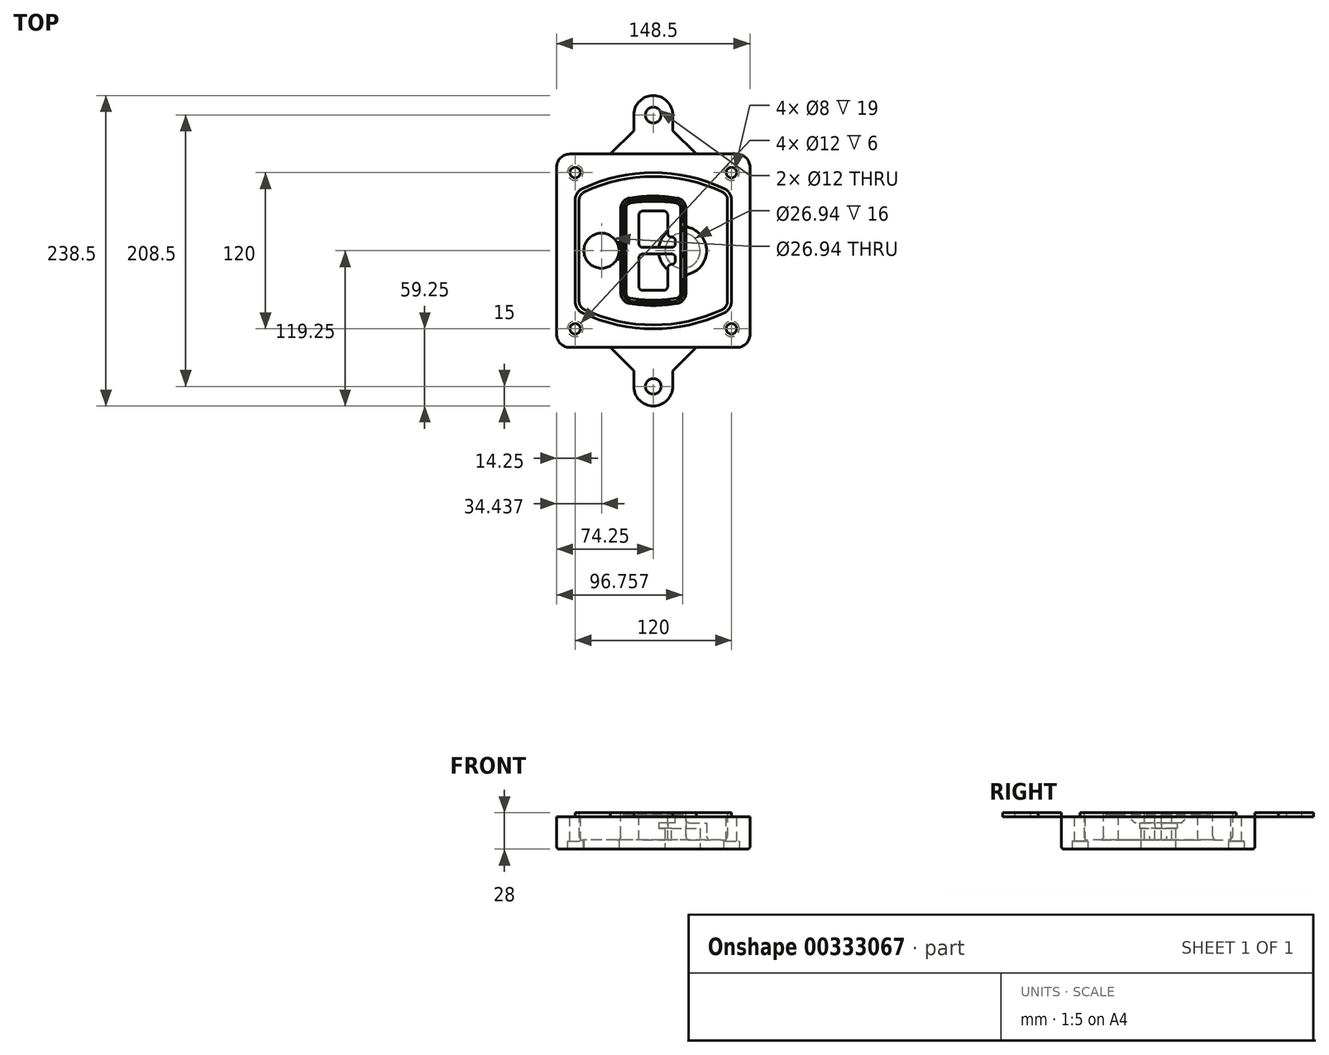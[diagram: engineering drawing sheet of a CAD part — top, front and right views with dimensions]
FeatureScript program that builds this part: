
annotation { "Feature Type Name" : "Feature", "Feature Type Description" : "" }
export const myFeature = defineFeature(function(context is Context, id is Id, definition is map)
    precondition{}
    {
        {
            var Q0;
            Q0=qCreatedBy(makeId("Top.planeOp"),FACE);
            var sketch = newSketch(context, id + "F0", { "sketchPlane" : qUnion([Q0])});
            skPoint(sketch, "E0.rect.middle", {"position": v(0, 0) * mm});
            skLineSegment(sketch, "E1.bottom", {"start": v(-64.25, -74.25) * mm, "end": v(64.25, -74.25) * mm});
            skLineSegment(sketch, "E1.top", {"start": v(-64.25, 74.25) * mm, "end": v(64.25, 74.25) * mm});
            skLineSegment(sketch, "E1.left", {"start": v(-74.25, -64.25) * mm, "end": v(-74.25, 64.25) * mm});
            skLineSegment(sketch, "E1.right", {"start": v(74.25, -64.25) * mm, "end": v(74.25, 64.25) * mm});
            skLineSegment(sketch, "E2", {"start": v(-74.25, 74.25) * mm, "end": v(74.25, -74.25) * mm, "construction": true});
            skLineSegment(sketch, "E3", {"start": v(74.25, 74.25) * mm, "end": v(-74.25, -74.25) * mm, "construction": true});
            skCircle(sketch, "E4", {"center": v(-60, 60) * mm, "radius": 4 * mm});
            skCircle(sketch, "E5", {"center": v(60, 60) * mm, "radius": 4 * mm});
            skCircle(sketch, "E6", {"center": v(60, -60) * mm, "radius": 4 * mm});
            skCircle(sketch, "E7", {"center": v(-60, -60) * mm, "radius": 4 * mm});
            skLineSegment(sketch, "E8", {"start": v(-60, 60) * mm, "end": v(60, 60) * mm, "construction": true});
            skLineSegment(sketch, "E9", {"start": v(60, 60) * mm, "end": v(60, -60) * mm, "construction": true});
            skLineSegment(sketch, "E10", {"start": v(60, -60) * mm, "end": v(-60, -60) * mm, "construction": true});
            skLineSegment(sketch, "E11", {"start": v(-60, -60) * mm, "end": v(-60, 60) * mm, "construction": true});
            skLineSegment(sketch, "E12", {"start": v(-60, 38.83) * mm, "end": v(-60, -38.83) * mm});
            skLineSegment(sketch, "E13", {"start": v(60, 38.83) * mm, "end": v(60, -38.83) * mm});
            skArc(sketch, "E14", {"start": v(54.26, 47.88) * mm, "mid": v(0, 60) * mm, "end": v(-54.26, 47.88) * mm});
            skArc(sketch, "E15", {"start": v(-54.26, -47.88) * mm, "mid": v(0, -60) * mm, "end": v(54.26, -47.88) * mm});
            skLineSegment(sketch, "E16", {"start": v(-60, 0) * mm, "end": v(60, 0) * mm, "construction": true});
            skPoint(sketch, "E17.visualSharp", {"position": v(-60, -45) * mm});
            skArc(sketch, "E17.filletArc", {"start": v(-60, -38.83) * mm, "mid": v(-58.44, -44.2) * mm, "end": v(-54.26, -47.88) * mm});
            skPoint(sketch, "E18.visualSharp", {"position": v(-60, 45) * mm});
            skArc(sketch, "E18.filletArc", {"start": v(-54.26, 47.88) * mm, "mid": v(-58.44, 44.2) * mm, "end": v(-60, 38.83) * mm});
            skPoint(sketch, "E19.visualSharp", {"position": v(60, 45) * mm});
            skArc(sketch, "E19.filletArc", {"start": v(60, 38.83) * mm, "mid": v(58.44, 44.2) * mm, "end": v(54.26, 47.88) * mm});
            skPoint(sketch, "E20.visualSharp", {"position": v(60, -45) * mm});
            skArc(sketch, "E20.filletArc", {"start": v(54.26, -47.88) * mm, "mid": v(58.44, -44.2) * mm, "end": v(60, -38.83) * mm});
            skPoint(sketch, "E21.visualSharp", {"position": v(-74.25, 74.25) * mm});
            skArc(sketch, "E21.filletArc", {"start": v(-64.25, 74.25) * mm, "mid": v(-71.32, 71.32) * mm, "end": v(-74.25, 64.25) * mm});
            skPoint(sketch, "E22.visualSharp", {"position": v(74.25, 74.25) * mm});
            skArc(sketch, "E22.filletArc", {"start": v(74.25, 64.25) * mm, "mid": v(71.32, 71.32) * mm, "end": v(64.25, 74.25) * mm});
            skPoint(sketch, "E23.visualSharp", {"position": v(74.25, -74.25) * mm});
            skArc(sketch, "E23.filletArc", {"start": v(64.25, -74.25) * mm, "mid": v(71.32, -71.32) * mm, "end": v(74.25, -64.25) * mm});
            skPoint(sketch, "E24.visualSharp", {"position": v(-74.25, -74.25) * mm});
            skArc(sketch, "E24.filletArc", {"start": v(-74.25, -64.25) * mm, "mid": v(-71.32, -71.32) * mm, "end": v(-64.25, -74.25) * mm});
            skArc(sketch, "E25.0", {"start": v(57, 38.83) * mm, "mid": v(55.9, 42.58) * mm, "end": v(52.98, 45.17) * mm});
            skLineSegment(sketch, "E25.1", {"start": v(57, 38.83) * mm, "end": v(57, -38.83) * mm});
            skArc(sketch, "E25.2", {"start": v(52.98, -45.17) * mm, "mid": v(55.9, -42.58) * mm, "end": v(57, -38.83) * mm});
            skArc(sketch, "E25.3", {"start": v(-52.98, -45.17) * mm, "mid": v(0, -57) * mm, "end": v(52.98, -45.17) * mm});
            skArc(sketch, "E25.4", {"start": v(-57, -38.83) * mm, "mid": v(-55.9, -42.58) * mm, "end": v(-52.98, -45.17) * mm});
            skArc(sketch, "E25.5", {"start": v(52.98, 45.17) * mm, "mid": v(0, 57) * mm, "end": v(-52.98, 45.17) * mm});
            skLineSegment(sketch, "E25.6", {"start": v(-57, 38.83) * mm, "end": v(-57, -38.83) * mm});
            skArc(sketch, "E25.7", {"start": v(-52.98, 45.17) * mm, "mid": v(-55.9, 42.58) * mm, "end": v(-57, 38.83) * mm});
            skArc(sketch, "E26.0", {"start": v(-55.96, 51.5) * mm, "mid": v(-61.82, 46.33) * mm, "end": v(-64, 38.83) * mm});
            skArc(sketch, "E26.1", {"start": v(55.96, 51.5) * mm, "mid": v(0, 64) * mm, "end": v(-55.96, 51.5) * mm});
            skArc(sketch, "E26.2", {"start": v(64, 38.83) * mm, "mid": v(61.82, 46.33) * mm, "end": v(55.96, 51.5) * mm});
            skLineSegment(sketch, "E26.3", {"start": v(64, 38.83) * mm, "end": v(64, -38.83) * mm});
            skArc(sketch, "E26.4", {"start": v(55.96, -51.5) * mm, "mid": v(61.82, -46.33) * mm, "end": v(64, -38.83) * mm});
            skLineSegment(sketch, "E26.5", {"start": v(-64, 38.83) * mm, "end": v(-64, -38.83) * mm});
            skArc(sketch, "E26.6", {"start": v(-55.96, -51.5) * mm, "mid": v(0, -64) * mm, "end": v(55.96, -51.5) * mm});
            skArc(sketch, "E26.7", {"start": v(-64, -38.83) * mm, "mid": v(-61.82, -46.33) * mm, "end": v(-55.96, -51.5) * mm});
            skSolve(sketch);
        }
        {
            var Q0;
            Q0=makeQuery(id+"F0.imprint","IMPRINT",FACE,{"disambiguationData":[TD([[makeQuery(id+"F0.imprint","IMPRINT",EDGE,{"derivedFrom":sQuery(id+"F0.wireOp",EDGE,"E1.bottom")}),1.0]])]});
            var Q1;
            Q1=makeQuery(id+"F0.imprint","IMPRINT",FACE,{"disambiguationData":[TD([[makeQuery(id+"F0.imprint","IMPRINT",EDGE,{"derivedFrom":sQuery(id+"F0.wireOp",EDGE,"E12")}),1.0]])]});
            var Q2;
            Q2=makeQuery(id+"F0.imprint","IMPRINT",FACE,{"disambiguationData":[TD([[makeQuery(id+"F0.imprint","IMPRINT",EDGE,{"derivedFrom":sQuery(id+"F0.wireOp",EDGE,"E25.0")}),1.0]])]});
            var Q3;
            Q3=makeQuery(id+"F0.imprint","IMPRINT",FACE,{"disambiguationData":[TD([[makeQuery(id+"F0.imprint","IMPRINT",EDGE,{"derivedFrom":sQuery(id+"F0.wireOp",EDGE,"E12")}),-1.0]])]});
            extrude(context, id + "F1", {"entities" : qUnion([Q0, Q1, Q2, Q3]), "oppositeDirection" : true, "depth" : 25 * mm});
        }
        {
            var Q0;
            Q0=makeQuery(id+"F0.imprint","IMPRINT",FACE,{"disambiguationData":[TD([[makeQuery(id+"F0.imprint","IMPRINT",EDGE,{"derivedFrom":sQuery(id+"F0.wireOp",EDGE,"E12")}),1.0]])]});
            extrude(context, id + "F2", {"entities" : qUnion([Q0]), "operationType" : NewBodyOperationType.ADD, "depth" : 3 * mm});
        }
        {
            var Q0;
            Q0=makeQuery(id+"F0.imprint","IMPRINT",FACE,{"disambiguationData":[TD([[makeQuery(id+"F0.imprint","IMPRINT",EDGE,{"derivedFrom":sQuery(id+"F0.wireOp",EDGE,"E25.0")}),1.0]])]});
            extrude(context, id + "F3", {"entities" : qUnion([Q0]), "operationType" : NewBodyOperationType.REMOVE, "oppositeDirection" : true, "depth" : 18 * mm});
        }
        {
            var Q0;
            Q0=makeQuery(id+"F2.opExtrude","CAP_FACE",FACE,{"disambiguationData":[OSD([sQuery(id+"F0.wireOp",EDGE,"E12"),sQuery(id+"F0.wireOp",EDGE,"E13"),sQuery(id+"F0.wireOp",EDGE,"E14"),sQuery(id+"F0.wireOp",EDGE,"E15"),sQuery(id+"F0.wireOp",EDGE,"E17.filletArc"),sQuery(id+"F0.wireOp",EDGE,"E18.filletArc"),sQuery(id+"F0.wireOp",EDGE,"E19.filletArc"),sQuery(id+"F0.wireOp",EDGE,"E20.filletArc"),sQuery(id+"F0.wireOp",EDGE,"E25.0"),sQuery(id+"F0.wireOp",EDGE,"E25.1"),sQuery(id+"F0.wireOp",EDGE,"E25.2"),sQuery(id+"F0.wireOp",EDGE,"E25.3"),sQuery(id+"F0.wireOp",EDGE,"E25.4"),sQuery(id+"F0.wireOp",EDGE,"E25.5"),sQuery(id+"F0.wireOp",EDGE,"E25.6"),sQuery(id+"F0.wireOp",EDGE,"E25.7")])],"isStart":false});
            var sketch = newSketch(context, id + "F4", { "sketchPlane" : qUnion([Q0])});
            skArc(sketch, "E27.0", {"start": v(-18.34, -40.45) * mm, "mid": v(0, -42) * mm, "end": v(18.34, -40.45) * mm});
            skArc(sketch, "E28.0", {"start": v(18.34, 40.45) * mm, "mid": v(0, 42) * mm, "end": v(-18.34, 40.45) * mm});
            skLineSegment(sketch, "E29", {"start": v(-25, 32.57) * mm, "end": v(-25, -32.57) * mm});
            skLineSegment(sketch, "E30", {"start": v(25, 32.57) * mm, "end": v(25, -32.57) * mm});
            skLineSegment(sketch, "E31", {"start": v(-25, 39.1) * mm, "end": v(25, 39.1) * mm, "construction": true});
            skLineSegment(sketch, "E32", {"start": v(-25, -39.1) * mm, "end": v(25, -39.1) * mm, "construction": true});
            skPoint(sketch, "E33.visualSharp", {"position": v(-25, 39.1) * mm});
            skArc(sketch, "E33.filletArc", {"start": v(-18.34, 40.45) * mm, "mid": v(-23.11, 37.73) * mm, "end": v(-25, 32.57) * mm});
            skPoint(sketch, "E34.visualSharp", {"position": v(25, 39.1) * mm});
            skArc(sketch, "E34.filletArc", {"start": v(25, 32.57) * mm, "mid": v(23.11, 37.73) * mm, "end": v(18.34, 40.45) * mm});
            skPoint(sketch, "E35.visualSharp", {"position": v(25, -39.1) * mm});
            skArc(sketch, "E35.filletArc", {"start": v(18.34, -40.45) * mm, "mid": v(23.11, -37.73) * mm, "end": v(25, -32.57) * mm});
            skPoint(sketch, "E36.visualSharp", {"position": v(-25, -39.1) * mm});
            skArc(sketch, "E36.filletArc", {"start": v(-25, -32.57) * mm, "mid": v(-23.11, -37.73) * mm, "end": v(-18.34, -40.45) * mm});
            skArc(sketch, "E37.0", {"start": v(52.98, 45.17) * mm, "mid": v(0, 57) * mm, "end": v(-52.98, 45.17) * mm});
            skArc(sketch, "E37.1", {"start": v(-52.98, 45.17) * mm, "mid": v(-55.9, 42.58) * mm, "end": v(-57, 38.83) * mm});
            skLineSegment(sketch, "E37.2", {"start": v(-57, 38.83) * mm, "end": v(-57, -38.83) * mm});
            skArc(sketch, "E37.3", {"start": v(-57, -38.83) * mm, "mid": v(-55.9, -42.58) * mm, "end": v(-52.98, -45.17) * mm});
            skArc(sketch, "E37.4", {"start": v(-52.98, -45.17) * mm, "mid": v(0, -57) * mm, "end": v(52.98, -45.17) * mm});
            skArc(sketch, "E37.5", {"start": v(52.98, -45.17) * mm, "mid": v(55.9, -42.58) * mm, "end": v(57, -38.83) * mm});
            skLineSegment(sketch, "E37.6", {"start": v(57, 38.83) * mm, "end": v(57, -38.83) * mm});
            skArc(sketch, "E37.7", {"start": v(57, 38.83) * mm, "mid": v(55.9, 42.58) * mm, "end": v(52.98, 45.17) * mm});
            skLineSegment(sketch, "E38.0", {"start": v(23, 32.57) * mm, "end": v(23, -32.57) * mm});
            skArc(sketch, "E38.1", {"start": v(18, -38.48) * mm, "mid": v(21.58, -36.44) * mm, "end": v(23, -32.57) * mm});
            skArc(sketch, "E38.2", {"start": v(-18, -38.48) * mm, "mid": v(0, -40) * mm, "end": v(18, -38.48) * mm});
            skArc(sketch, "E38.3", {"start": v(-23, -32.57) * mm, "mid": v(-21.58, -36.44) * mm, "end": v(-18, -38.48) * mm});
            skLineSegment(sketch, "E38.4", {"start": v(-23, 32.57) * mm, "end": v(-23, -32.57) * mm});
            skArc(sketch, "E38.5", {"start": v(23, 32.57) * mm, "mid": v(21.58, 36.44) * mm, "end": v(18, 38.48) * mm});
            skArc(sketch, "E38.6", {"start": v(-18, 38.48) * mm, "mid": v(-21.58, 36.44) * mm, "end": v(-23, 32.57) * mm});
            skArc(sketch, "E38.7", {"start": v(18, 38.48) * mm, "mid": v(0, 40) * mm, "end": v(-18, 38.48) * mm});
            skArc(sketch, "E39.0", {"start": v(21, 32.57) * mm, "mid": v(20.06, 35.15) * mm, "end": v(17.67, 36.5) * mm});
            skLineSegment(sketch, "E39.1", {"start": v(21, 32.57) * mm, "end": v(21, -32.57) * mm});
            skArc(sketch, "E39.2", {"start": v(17.67, -36.5) * mm, "mid": v(20.06, -35.15) * mm, "end": v(21, -32.57) * mm});
            skArc(sketch, "E39.3", {"start": v(-17.67, -36.5) * mm, "mid": v(0, -38) * mm, "end": v(17.67, -36.5) * mm});
            skArc(sketch, "E39.4", {"start": v(-21, -32.57) * mm, "mid": v(-20.06, -35.15) * mm, "end": v(-17.67, -36.5) * mm});
            skArc(sketch, "E39.5", {"start": v(17.67, 36.5) * mm, "mid": v(0, 38) * mm, "end": v(-17.67, 36.5) * mm});
            skLineSegment(sketch, "E39.6", {"start": v(-21, 32.57) * mm, "end": v(-21, -32.57) * mm});
            skArc(sketch, "E39.7", {"start": v(-17.67, 36.5) * mm, "mid": v(-20.06, 35.15) * mm, "end": v(-21, 32.57) * mm});
            skLineSegment(sketch, "E40", {"start": v(-25, 0) * mm, "end": v(25, 0) * mm, "construction": true});
            skLineSegment(sketch, "E41", {"start": v(-11, 5.5) * mm, "end": v(-11, 27.5) * mm});
            skLineSegment(sketch, "E42", {"start": v(-8, 30.5) * mm, "end": v(8, 30.5) * mm});
            skLineSegment(sketch, "E43", {"start": v(11, 27.5) * mm, "end": v(11, 13.5) * mm});
            skLineSegment(sketch, "E44", {"start": v(14, 10.5) * mm, "end": v(14, 10.5) * mm});
            skLineSegment(sketch, "E45", {"start": v(17, 7.5) * mm, "end": v(17, 5.5) * mm});
            skLineSegment(sketch, "E46", {"start": v(14, 2.5) * mm, "end": v(-8, 2.5) * mm});
            skPoint(sketch, "E47.visualSharp", {"position": v(-11, 30.5) * mm});
            skArc(sketch, "E47.filletArc", {"start": v(-8, 30.5) * mm, "mid": v(-10.12, 29.62) * mm, "end": v(-11, 27.5) * mm});
            skPoint(sketch, "E48.visualSharp", {"position": v(11, 30.5) * mm});
            skArc(sketch, "E48.filletArc", {"start": v(11, 27.5) * mm, "mid": v(10.12, 29.62) * mm, "end": v(8, 30.5) * mm});
            skPoint(sketch, "E49.visualSharp", {"position": v(11, 10.5) * mm});
            skArc(sketch, "E49.filletArc", {"start": v(11, 13.5) * mm, "mid": v(11.88, 11.38) * mm, "end": v(14, 10.5) * mm});
            skPoint(sketch, "E50.visualSharp", {"position": v(17, 10.5) * mm});
            skArc(sketch, "E50.filletArc", {"start": v(17, 7.5) * mm, "mid": v(16.12, 9.62) * mm, "end": v(14, 10.5) * mm});
            skPoint(sketch, "E51.visualSharp", {"position": v(17, 2.5) * mm});
            skArc(sketch, "E51.filletArc", {"start": v(14, 2.5) * mm, "mid": v(16.12, 3.38) * mm, "end": v(17, 5.5) * mm});
            skPoint(sketch, "E52.visualSharp", {"position": v(-11, 2.5) * mm});
            skArc(sketch, "E52.filletArc", {"start": v(-11, 5.5) * mm, "mid": v(-10.12, 3.38) * mm, "end": v(-8, 2.5) * mm});
            skLineSegment(sketch, "E53.0.MirrorCS", {"start": v(14, -2.5) * mm, "end": v(-8, -2.5) * mm});
            skArc(sketch, "E54.0.MirrorCS", {"start": v(-11, -5.5) * mm, "mid": v(-10.12, -3.38) * mm, "end": v(-8, -2.5) * mm});
            skLineSegment(sketch, "E55.0.MirrorCS", {"start": v(-11, -5.5) * mm, "end": v(-11, -27.5) * mm});
            skArc(sketch, "E56.0.MirrorCS", {"start": v(-8, -30.5) * mm, "mid": v(-10.12, -29.62) * mm, "end": v(-11, -27.5) * mm});
            skLineSegment(sketch, "E57.0.MirrorCS", {"start": v(-8, -30.5) * mm, "end": v(8, -30.5) * mm});
            skArc(sketch, "E58.0.MirrorCS", {"start": v(11, -27.5) * mm, "mid": v(10.12, -29.62) * mm, "end": v(8, -30.5) * mm});
            skLineSegment(sketch, "E59.0.MirrorCS", {"start": v(11, -27.5) * mm, "end": v(11, -13.5) * mm});
            skArc(sketch, "E60.0.MirrorCS", {"start": v(11, -13.5) * mm, "mid": v(11.88, -11.38) * mm, "end": v(14, -10.5) * mm});
            skArc(sketch, "E61.0.MirrorCS", {"start": v(17, -7.5) * mm, "mid": v(16.12, -9.62) * mm, "end": v(14, -10.5) * mm});
            skLineSegment(sketch, "E62.0.MirrorCS", {"start": v(17, -7.5) * mm, "end": v(17, -5.5) * mm});
            skArc(sketch, "E63.0.MirrorCS", {"start": v(14, -2.5) * mm, "mid": v(16.12, -3.38) * mm, "end": v(17, -5.5) * mm});
            skSolve(sketch);
        }
        {
            var Q0;
            Q0=makeQuery(id+"F4.imprint","IMPRINT",FACE,{"disambiguationData":[TD([[makeQuery(id+"F4.imprint","IMPRINT",EDGE,{"derivedFrom":sQuery(id+"F4.wireOp",EDGE,"E27.0")}),1.0]])]});
            var Q1;
            Q1=makeQuery(id+"F4.imprint","IMPRINT",FACE,{"disambiguationData":[TD([[makeQuery(id+"F4.imprint","IMPRINT",EDGE,{"derivedFrom":sQuery(id+"F4.wireOp",EDGE,"E38.0")}),-1.0]])]});
            var Q2;
            Q2=makeQuery(id+"F4.imprint","IMPRINT",FACE,{"disambiguationData":[TD([[makeQuery(id+"F4.imprint","IMPRINT",EDGE,{"derivedFrom":sQuery(id+"F4.wireOp",EDGE,"E39.0")}),1.0]])]});
            extrude(context, id + "F5", {"entities" : qUnion([Q0, Q1, Q2]), "operationType" : NewBodyOperationType.ADD, "endBound" : BoundingType.UP_TO_NEXT, "oppositeDirection" : true, "depth" : 25 * mm});
        }
        {
            var Q0;
            Q0=makeQuery(id+"F4.imprint","IMPRINT",FACE,{"disambiguationData":[TD([[makeQuery(id+"F4.imprint","IMPRINT",EDGE,{"derivedFrom":sQuery(id+"F4.wireOp",EDGE,"E38.0")}),-1.0]])]});
            extrude(context, id + "F6", {"entities" : qUnion([Q0]), "operationType" : NewBodyOperationType.REMOVE, "oppositeDirection" : true, "depth" : 2 * mm});
        }
        {
            var Q0;
            Q0=makeQuery(id+"F1.opExtrude","CAP_FACE",FACE,{"disambiguationData":[OSD([sQuery(id+"F0.wireOp",EDGE,"E1.bottom"),sQuery(id+"F0.wireOp",EDGE,"E1.top"),sQuery(id+"F0.wireOp",EDGE,"E1.left"),sQuery(id+"F0.wireOp",EDGE,"E1.right"),sQuery(id+"F0.wireOp",EDGE,"E4"),sQuery(id+"F0.wireOp",EDGE,"E5"),sQuery(id+"F0.wireOp",EDGE,"E6"),sQuery(id+"F0.wireOp",EDGE,"E7"),sQuery(id+"F0.wireOp",EDGE,"E21.filletArc"),sQuery(id+"F0.wireOp",EDGE,"E22.filletArc"),sQuery(id+"F0.wireOp",EDGE,"E23.filletArc"),sQuery(id+"F0.wireOp",EDGE,"E24.filletArc")])],"isStart":false});
            var sketch = newSketch(context, id + "F7", { "sketchPlane" : qUnion([Q0])});
            skCircle(sketch, "E64", {"center": v(22.5, 0) * mm, "radius": 13.47 * mm});
            skCircle(sketch, "E65", {"center": v(-39.81, 0) * mm, "radius": 13.47 * mm});
            skLineSegment(sketch, "E66", {"start": v(74.25, 0) * mm, "end": v(-74.25, 0) * mm});
            skCircle(sketch, "E67", {"center": v(22.5, 0) * mm, "radius": 18.47 * mm});
            skCircle(sketch, "E68", {"center": v(60, -60) * mm, "radius": 6 * mm});
            skCircle(sketch, "E69", {"center": v(-60, -60) * mm, "radius": 6 * mm});
            skCircle(sketch, "E70", {"center": v(-60, 60) * mm, "radius": 6 * mm});
            skCircle(sketch, "E71", {"center": v(60, 60) * mm, "radius": 6 * mm});
            skSolve(sketch);
        }
        {
            var Q0;
            {var subQ1=sQuery(id+"F7.wireOp",EDGE,"E66");var subQ4=sQuery(id+"F7.wireOp",EDGE,"E64");var subQ6=makeQuery(id+"F7.imprint","INTERSECT",VERTEX,{"disambiguationData":[OD(0.0)],"derivedFrom":[subQ4,subQ1]});Q0=makeQuery(id+"F7.imprint","IMPRINT",FACE,{"disambiguationData":[TD([[makeQuery(id+"F7.imprint","IMPRINT",EDGE,{"disambiguationData":[TD([[subQ6,-1.0]])],"derivedFrom":subQ4}),-1.0]])]});}
            var Q1;
            {var subQ0=sQuery(id+"F7.wireOp",EDGE,"E66");var subQ1=sQuery(id+"F7.wireOp",EDGE,"E64");var subQ3=makeQuery(id+"F7.imprint","INTERSECT",VERTEX,{"disambiguationData":[OD(0.0)],"derivedFrom":[subQ1,subQ0]});Q1=makeQuery(id+"F7.imprint","IMPRINT",FACE,{"disambiguationData":[TD([[makeQuery(id+"F7.imprint","IMPRINT",EDGE,{"disambiguationData":[TD([[subQ3,-1.0]])],"derivedFrom":subQ1}),1.0]])]});}
            var Q2;
            {var subQ0=sQuery(id+"F7.wireOp",EDGE,"E66");var subQ1=sQuery(id+"F7.wireOp",EDGE,"E64");var subQ3=makeQuery(id+"F7.imprint","INTERSECT",VERTEX,{"disambiguationData":[OD(0.0)],"derivedFrom":[subQ1,subQ0]});Q2=makeQuery(id+"F7.imprint","IMPRINT",FACE,{"disambiguationData":[TD([[makeQuery(id+"F7.imprint","IMPRINT",EDGE,{"disambiguationData":[TD([[subQ3,1.0]])],"derivedFrom":subQ1}),1.0]])]});}
            var Q3;
            {var subQ1=sQuery(id+"F7.wireOp",EDGE,"E66");var subQ4=sQuery(id+"F7.wireOp",EDGE,"E64");var subQ6=makeQuery(id+"F7.imprint","INTERSECT",VERTEX,{"disambiguationData":[OD(0.0)],"derivedFrom":[subQ4,subQ1]});Q3=makeQuery(id+"F7.imprint","IMPRINT",FACE,{"disambiguationData":[TD([[makeQuery(id+"F7.imprint","IMPRINT",EDGE,{"disambiguationData":[TD([[subQ6,1.0]])],"derivedFrom":subQ4}),-1.0]])]});}
            extrude(context, id + "F8", {"entities" : qUnion([Q0, Q1, Q2, Q3]), "operationType" : NewBodyOperationType.ADD, "oppositeDirection" : true, "depth" : 20 * mm});
        }
        {
            var Q0;
            {var subQ0=sQuery(id+"F7.wireOp",EDGE,"E66");var subQ1=sQuery(id+"F7.wireOp",EDGE,"E64");var subQ3=makeQuery(id+"F7.imprint","INTERSECT",VERTEX,{"disambiguationData":[OD(0.0)],"derivedFrom":[subQ1,subQ0]});Q0=makeQuery(id+"F7.imprint","IMPRINT",FACE,{"disambiguationData":[TD([[makeQuery(id+"F7.imprint","IMPRINT",EDGE,{"disambiguationData":[TD([[subQ3,-1.0]])],"derivedFrom":subQ1}),1.0]])]});}
            var Q1;
            {var subQ0=sQuery(id+"F7.wireOp",EDGE,"E66");var subQ1=sQuery(id+"F7.wireOp",EDGE,"E64");var subQ3=makeQuery(id+"F7.imprint","INTERSECT",VERTEX,{"disambiguationData":[OD(0.0)],"derivedFrom":[subQ1,subQ0]});Q1=makeQuery(id+"F7.imprint","IMPRINT",FACE,{"disambiguationData":[TD([[makeQuery(id+"F7.imprint","IMPRINT",EDGE,{"disambiguationData":[TD([[subQ3,1.0]])],"derivedFrom":subQ1}),1.0]])]});}
            extrude(context, id + "F9", {"entities" : qUnion([Q0, Q1]), "operationType" : NewBodyOperationType.REMOVE, "oppositeDirection" : true, "depth" : 16 * mm});
        }
        {
            var Q0;
            {var subQ0=sQuery(id+"F7.wireOp",EDGE,"E66");var subQ1=sQuery(id+"F7.wireOp",EDGE,"E65");var subQ3=makeQuery(id+"F7.imprint","INTERSECT",VERTEX,{"disambiguationData":[OD(0.0)],"derivedFrom":[subQ1,subQ0]});Q0=makeQuery(id+"F7.imprint","IMPRINT",FACE,{"disambiguationData":[TD([[makeQuery(id+"F7.imprint","IMPRINT",EDGE,{"disambiguationData":[TD([[subQ3,-1.0]])],"derivedFrom":subQ1}),1.0]])]});}
            var Q1;
            {var subQ0=sQuery(id+"F7.wireOp",EDGE,"E66");var subQ1=sQuery(id+"F7.wireOp",EDGE,"E65");var subQ3=makeQuery(id+"F7.imprint","INTERSECT",VERTEX,{"disambiguationData":[OD(0.0)],"derivedFrom":[subQ1,subQ0]});Q1=makeQuery(id+"F7.imprint","IMPRINT",FACE,{"disambiguationData":[TD([[makeQuery(id+"F7.imprint","IMPRINT",EDGE,{"disambiguationData":[TD([[subQ3,1.0]])],"derivedFrom":subQ1}),1.0]])]});}
            extrude(context, id + "F10", {"entities" : qUnion([Q0, Q1]), "operationType" : NewBodyOperationType.REMOVE, "oppositeDirection" : true, "depth" : 25 * mm});
        }
        {
            var Q0;
            Q0=makeQuery(id+"F7.imprint","IMPRINT",FACE,{"disambiguationData":[TD([[makeQuery(id+"F7.imprint","IMPRINT",EDGE,{"derivedFrom":sQuery(id+"F7.wireOp",EDGE,"E68")}),1.0]])]});
            var Q1;
            Q1=makeQuery(id+"F7.imprint","IMPRINT",FACE,{"disambiguationData":[TD([[makeQuery(id+"F7.imprint","IMPRINT",EDGE,{"derivedFrom":makeQuery(id+"F1.opExtrude","CAP_EDGE",EDGE,{"disambiguationData":[OSD([sQuery(id+"F0.wireOp",EDGE,"E5")])],"isStart":false})}),-1.0]])]});
            var Q2;
            Q2=makeQuery(id+"F7.imprint","IMPRINT",FACE,{"disambiguationData":[TD([[makeQuery(id+"F7.imprint","IMPRINT",EDGE,{"derivedFrom":sQuery(id+"F7.wireOp",EDGE,"E69")}),1.0]])]});
            var Q3;
            Q3=makeQuery(id+"F7.imprint","IMPRINT",FACE,{"disambiguationData":[TD([[makeQuery(id+"F7.imprint","IMPRINT",EDGE,{"derivedFrom":makeQuery(id+"F1.opExtrude","CAP_EDGE",EDGE,{"disambiguationData":[OSD([sQuery(id+"F0.wireOp",EDGE,"E4")])],"isStart":false})}),-1.0]])]});
            var Q4;
            Q4=makeQuery(id+"F7.imprint","IMPRINT",FACE,{"disambiguationData":[TD([[makeQuery(id+"F7.imprint","IMPRINT",EDGE,{"derivedFrom":sQuery(id+"F7.wireOp",EDGE,"E70")}),1.0]])]});
            var Q5;
            Q5=makeQuery(id+"F7.imprint","IMPRINT",FACE,{"disambiguationData":[TD([[makeQuery(id+"F7.imprint","IMPRINT",EDGE,{"derivedFrom":makeQuery(id+"F1.opExtrude","CAP_EDGE",EDGE,{"disambiguationData":[OSD([sQuery(id+"F0.wireOp",EDGE,"E7")])],"isStart":false})}),-1.0]])]});
            var Q6;
            Q6=makeQuery(id+"F7.imprint","IMPRINT",FACE,{"disambiguationData":[TD([[makeQuery(id+"F7.imprint","IMPRINT",EDGE,{"derivedFrom":sQuery(id+"F7.wireOp",EDGE,"E71")}),1.0]])]});
            var Q7;
            Q7=makeQuery(id+"F7.imprint","IMPRINT",FACE,{"disambiguationData":[TD([[makeQuery(id+"F7.imprint","IMPRINT",EDGE,{"derivedFrom":makeQuery(id+"F1.opExtrude","CAP_EDGE",EDGE,{"disambiguationData":[OSD([sQuery(id+"F0.wireOp",EDGE,"E6")])],"isStart":false})}),-1.0]])]});
            extrude(context, id + "F11", {"entities" : qUnion([Q0, Q1, Q2, Q3, Q4, Q5, Q6, Q7]), "operationType" : NewBodyOperationType.REMOVE, "oppositeDirection" : true, "depth" : 6 * mm});
        }
        {
            var Q0;
            Q0=makeQuery(id+"F9.boolean.opBoolean","COPY",FACE,{"derivedFrom":makeQuery(id+"F9.opExtrude","CAP_FACE",FACE,{"disambiguationData":[OSD([sQuery(id+"F7.wireOp",EDGE,"E64")])],"isStart":false})});
            var sketch = newSketch(context, id + "F12", { "sketchPlane" : qUnion([Q0])});
            skArc(sketch, "E72.0", {"start": v(11, 14.45) * mm, "mid": v(6.45, 9.13) * mm, "end": v(4.2, 2.5) * mm});
            skArc(sketch, "E72.1", {"start": v(4.2, -2.5) * mm, "mid": v(6.45, -9.13) * mm, "end": v(11, -14.45) * mm});
            skLineSegment(sketch, "E73", {"start": v(4.2, -2.5) * mm, "end": v(14, -2.5) * mm});
            skLineSegment(sketch, "E74.0", {"start": v(14, 2.5) * mm, "end": v(4.2, 2.5) * mm});
            skArc(sketch, "E74.1", {"start": v(14, 2.5) * mm, "mid": v(16.12, 3.38) * mm, "end": v(17, 5.5) * mm});
            skLineSegment(sketch, "E74.2", {"start": v(17, 7.5) * mm, "end": v(17, 5.5) * mm});
            skArc(sketch, "E74.3", {"start": v(17, 7.5) * mm, "mid": v(16.12, 9.62) * mm, "end": v(14, 10.5) * mm});
            skArc(sketch, "E74.4", {"start": v(11, 13.5) * mm, "mid": v(11.88, 11.38) * mm, "end": v(14, 10.5) * mm});
            skLineSegment(sketch, "E74.5", {"start": v(11, 14.45) * mm, "end": v(11, 13.5) * mm});
            skLineSegment(sketch, "E74.7", {"start": v(14, -2.5) * mm, "end": v(4.2, -2.5) * mm});
            skArc(sketch, "E74.8", {"start": v(14, -2.5) * mm, "mid": v(16.12, -3.38) * mm, "end": v(17, -5.5) * mm});
            skLineSegment(sketch, "E74.9", {"start": v(17, -7.5) * mm, "end": v(17, -5.5) * mm});
            skArc(sketch, "E74.10", {"start": v(17, -7.5) * mm, "mid": v(16.12, -9.62) * mm, "end": v(14, -10.5) * mm});
            skArc(sketch, "E74.11", {"start": v(11, -13.5) * mm, "mid": v(11.88, -11.38) * mm, "end": v(14, -10.5) * mm});
            skLineSegment(sketch, "E74.12", {"start": v(11, -14.45) * mm, "end": v(11, -13.5) * mm});
            skPoint(sketch, "E75.orphan", {"position": v(11, -27.5) * mm});
            skPoint(sketch, "E76.orphan", {"position": v(-8, -2.5) * mm});
            skPoint(sketch, "E77.orphan", {"position": v(-8, 2.5) * mm});
            skPoint(sketch, "E78.orphan", {"position": v(11, 27.5) * mm});
            skSolve(sketch);
        }
        {
            var Q0;
            {var subQ7=sQuery(id+"F12.wireOp",EDGE,"E72.0");var subQ14=sQuery(id+"F12.wireOp",EDGE,"E72.1");var subQ16=sQuery(id+"F12.wireOp",EDGE,"E74.1");var subQ18=sQuery(id+"F12.wireOp",EDGE,"E74.8");Q0=qUnion([makeQuery(id+"F12.imprint","IMPRINT",FACE,{"disambiguationData":[TD([[makeQuery(id+"F12.imprint","IMPRINT",EDGE,{"derivedFrom":subQ7}),1.0]])]}),makeQuery(id+"F12.imprint","IMPRINT",FACE,{"disambiguationData":[TD([[makeQuery(id+"F12.imprint","IMPRINT",EDGE,{"derivedFrom":subQ14}),1.0]])]}),makeQuery(id+"F12.imprint","IMPRINT",FACE,{"disambiguationData":[TD([[makeQuery(id+"F12.imprint","IMPRINT",EDGE,{"derivedFrom":subQ16}),1.0]])]}),makeQuery(id+"F12.imprint","IMPRINT",FACE,{"disambiguationData":[TD([[makeQuery(id+"F12.imprint","IMPRINT",EDGE,{"derivedFrom":subQ18}),-1.0]])]})]);}
            var Q1;
            Q1=makeQuery(id+"F5.boolean.opBoolean","SPLIT",FACE,{"disambiguationData":[TD([makeQuery(id+"F5.opExtrude","SWEPT_FACE",FACE,{"disambiguationData":[OSD([sQuery(id+"F4.wireOp",EDGE,"E41")])]})])],"derivedFrom":makeQuery(id+"F3.boolean.opBoolean","COPY",FACE,{"derivedFrom":makeQuery(id+"F3.opExtrude","CAP_FACE",FACE,{"disambiguationData":[OSD([sQuery(id+"F0.wireOp",EDGE,"E25.0"),sQuery(id+"F0.wireOp",EDGE,"E25.1"),sQuery(id+"F0.wireOp",EDGE,"E25.2"),sQuery(id+"F0.wireOp",EDGE,"E25.3"),sQuery(id+"F0.wireOp",EDGE,"E25.4"),sQuery(id+"F0.wireOp",EDGE,"E25.5"),sQuery(id+"F0.wireOp",EDGE,"E25.6"),sQuery(id+"F0.wireOp",EDGE,"E25.7")])],"isStart":false})})});
            extrude(context, id + "F13", {"entities" : qUnion([Q0]), "operationType" : NewBodyOperationType.REMOVE, "endBound" : BoundingType.UP_TO_SURFACE, "endBoundEntityFace" : qUnion([Q1]), "depth" : 25 * mm});
        }
        {
            var Q0;
            Q0=makeQuery(id+"F3.boolean.opBoolean","COPY",EDGE,{"derivedFrom":makeQuery(id+"F3.opExtrude","CAP_EDGE",EDGE,{"disambiguationData":[OSD([sQuery(id+"F0.wireOp",EDGE,"E25.6")])],"isStart":false})});
            var Q1;
            Q1=makeQuery(id+"F8.boolean.opBoolean","INTERSECT",EDGE,{"derivedFrom":[makeQuery(id+"F5.opExtrude","SWEPT_FACE",FACE,{"disambiguationData":[OSD([sQuery(id+"F4.wireOp",EDGE,"E30")])]}),makeQuery(id+"F8.opExtrude","CAP_FACE",FACE,{"disambiguationData":[OSD([sQuery(id+"F7.wireOp",EDGE,"E67")])],"isStart":false})]});
            var Q2;
            Q2=makeQuery(id+"F8.boolean.opBoolean","INTERSECT",EDGE,{"disambiguationData":[OD(1.0)],"derivedFrom":[makeQuery(id+"F5.opExtrude","SWEPT_FACE",FACE,{"disambiguationData":[OSD([sQuery(id+"F4.wireOp",EDGE,"E30")])]}),makeQuery(id+"F8.opExtrude","SWEPT_FACE",FACE,{"disambiguationData":[OSD([sQuery(id+"F7.wireOp",EDGE,"E67")])]})]});
            var Q3;
            {var subQ0=sQuery(id+"F4.wireOp",EDGE,"E30");Q3=makeQuery(id+"F8.boolean.opBoolean","SPLIT",EDGE,{"disambiguationData":[TD([makeQuery(id+"F5.opExtrude","SWEPT_FACE",FACE,{"disambiguationData":[OSD([sQuery(id+"F4.wireOp",EDGE,"E35.filletArc")])]})])],"derivedFrom":makeQuery(id+"F5.opExtrude","CAP_EDGE",EDGE,{"disambiguationData":[OSD([subQ0])],"isStart":false})});}
            var Q4;
            {var subQ0=sQuery(id+"F0.wireOp",EDGE,"E25.7");var subQ1=sQuery(id+"F0.wireOp",EDGE,"E25.1");var subQ2=sQuery(id+"F0.wireOp",EDGE,"E25.6");var subQ3=sQuery(id+"F0.wireOp",EDGE,"E25.5");var subQ4=sQuery(id+"F0.wireOp",EDGE,"E25.4");var subQ5=sQuery(id+"F0.wireOp",EDGE,"E25.0");var subQ6=sQuery(id+"F0.wireOp",EDGE,"E25.2");var subQ7=sQuery(id+"F0.wireOp",EDGE,"E25.3");Q4=makeQuery(id+"F8.boolean.opBoolean","INTERSECT",EDGE,{"derivedFrom":[makeQuery(id+"F5.boolean.opBoolean","SPLIT",FACE,{"disambiguationData":[TD([makeQuery(id+"F2.opExtrude","SWEPT_FACE",FACE,{"disambiguationData":[OSD([subQ5])]})])],"derivedFrom":makeQuery(id+"F3.boolean.opBoolean","COPY",FACE,{"derivedFrom":makeQuery(id+"F3.opExtrude","CAP_FACE",FACE,{"disambiguationData":[OSD([subQ5,subQ1,subQ6,subQ7,subQ4,subQ3,subQ2,subQ0])],"isStart":false})})}),makeQuery(id+"F8.opExtrude","SWEPT_FACE",FACE,{"disambiguationData":[OSD([sQuery(id+"F7.wireOp",EDGE,"E67")])]})]});}
            var Q5;
            Q5=makeQuery(id+"F8.boolean.opBoolean","INTERSECT",EDGE,{"disambiguationData":[OD(0.0)],"derivedFrom":[makeQuery(id+"F5.opExtrude","SWEPT_FACE",FACE,{"disambiguationData":[OSD([sQuery(id+"F4.wireOp",EDGE,"E30")])]}),makeQuery(id+"F8.opExtrude","SWEPT_FACE",FACE,{"disambiguationData":[OSD([sQuery(id+"F7.wireOp",EDGE,"E67")])]})]});
            fillet(context, id + "F14", {"entities" : qUnion([Q0, Q1, Q2, Q3, Q4, Q5]), "radius" : 3 * mm, "tangentPropagation" : true, "allowEdgeOverflow" : false});
        }
        {
            var Q0;
            Q0=makeQuery(id+"F1.opExtrude","CAP_EDGE",EDGE,{"disambiguationData":[OSD([sQuery(id+"F0.wireOp",EDGE,"E1.bottom")])],"isStart":false});
            fillet(context, id + "F15", {"entities" : qUnion([Q0]), "radius" : 2 * mm, "tangentPropagation" : true, "allowEdgeOverflow" : false});
        }
        {
            var Q0;
            {var subQ0=sQuery(id+"F0.wireOp",EDGE,"E21.filletArc");var subQ1=sQuery(id+"F0.wireOp",EDGE,"E7");var subQ2=sQuery(id+"F0.wireOp",EDGE,"E6");var subQ3=sQuery(id+"F0.wireOp",EDGE,"E5");var subQ4=sQuery(id+"F0.wireOp",EDGE,"E4");var subQ5=sQuery(id+"F0.wireOp",EDGE,"E22.filletArc");var subQ6=sQuery(id+"F0.wireOp",EDGE,"E1.bottom");var subQ7=sQuery(id+"F0.wireOp",EDGE,"E1.right");var subQ8=sQuery(id+"F0.wireOp",EDGE,"E1.top");var subQ9=sQuery(id+"F0.wireOp",EDGE,"E1.left");var subQ10=sQuery(id+"F0.wireOp",EDGE,"E23.filletArc");var subQ11=sQuery(id+"F0.wireOp",EDGE,"E24.filletArc");Q0=makeQuery(id+"F2.boolean.opBoolean","SPLIT",FACE,{"disambiguationData":[TD([makeQuery(id+"F1.opExtrude","SWEPT_FACE",FACE,{"disambiguationData":[OSD([subQ6])]})])],"derivedFrom":makeQuery(id+"F1.opExtrude","CAP_FACE",FACE,{"disambiguationData":[OSD([subQ6,subQ8,subQ9,subQ7,subQ4,subQ3,subQ2,subQ1,subQ0,subQ5,subQ10,subQ11])],"isStart":true})});}
            var sketch = newSketch(context, id + "F16", { "sketchPlane" : qUnion([Q0])});
            skLineSegment(sketch, "E79", {"start": v(0, 74.25) * mm, "end": v(0, 104.25) * mm, "construction": true});
            skLineSegment(sketch, "E80", {"start": v(-33, 74.25) * mm, "end": v(-15, 92.25) * mm});
            skLineSegment(sketch, "E81", {"start": v(-15, 92.25) * mm, "end": v(-15, 104.25) * mm});
            skLineSegment(sketch, "E82", {"start": v(15, 92.25) * mm, "end": v(15, 104.25) * mm});
            skLineSegment(sketch, "E83", {"start": v(15, 92.25) * mm, "end": v(33, 74.25) * mm});
            skArc(sketch, "E84", {"start": v(15, 104.25) * mm, "mid": v(0, 119.25) * mm, "end": v(-15, 104.25) * mm});
            skCircle(sketch, "E85", {"center": v(0, 104.25) * mm, "radius": 6 * mm});
            skLineSegment(sketch, "E86", {"start": v(-74.25, 0) * mm, "end": v(74.25, 0) * mm});
            skLineSegment(sketch, "E87.MirrorCS", {"start": v(15, -92.25) * mm, "end": v(33, -74.25) * mm});
            skLineSegment(sketch, "E88.MirrorCS", {"start": v(15, -92.25) * mm, "end": v(15, -104.25) * mm});
            skArc(sketch, "E89.MirrorCS", {"start": v(15, -104.25) * mm, "mid": v(0, -119.25) * mm, "end": v(-15, -104.25) * mm});
            skLineSegment(sketch, "E90.MirrorCS", {"start": v(-15, -92.25) * mm, "end": v(-15, -104.25) * mm});
            skLineSegment(sketch, "E91.MirrorCS", {"start": v(-33, -74.25) * mm, "end": v(-15, -92.25) * mm});
            skCircle(sketch, "E92.MirrorC", {"center": v(0, -104.25) * mm, "radius": 6 * mm});
            skLineSegment(sketch, "E93.MirrorCS", {"start": v(0, -74.25) * mm, "end": v(0, -104.25) * mm, "construction": true});
            skSolve(sketch);
        }
        {
            var Q0;
            {var subQ1=sQuery(id+"F16.wireOp",EDGE,"E80");Q0=makeQuery(id+"F16.imprint","IMPRINT",FACE,{"disambiguationData":[TD([[makeQuery(id+"F16.imprint","IMPRINT",EDGE,{"derivedFrom":subQ1}),-1.0]])]});}
            var Q1;
            {var subQ0=sQuery(id+"F16.wireOp",EDGE,"E87.MirrorCS");Q1=makeQuery(id+"F16.imprint","IMPRINT",FACE,{"disambiguationData":[TD([[makeQuery(id+"F16.imprint","IMPRINT",EDGE,{"derivedFrom":subQ0}),1.0]])]});}
            var Q2;
            Q2=makeQuery(id+"F2.opExtrude","CAP_FACE",FACE,{"disambiguationData":[OSD([sQuery(id+"F0.wireOp",EDGE,"E12"),sQuery(id+"F0.wireOp",EDGE,"E13"),sQuery(id+"F0.wireOp",EDGE,"E14"),sQuery(id+"F0.wireOp",EDGE,"E15"),sQuery(id+"F0.wireOp",EDGE,"E17.filletArc"),sQuery(id+"F0.wireOp",EDGE,"E18.filletArc"),sQuery(id+"F0.wireOp",EDGE,"E19.filletArc"),sQuery(id+"F0.wireOp",EDGE,"E20.filletArc"),sQuery(id+"F0.wireOp",EDGE,"E25.0"),sQuery(id+"F0.wireOp",EDGE,"E25.1"),sQuery(id+"F0.wireOp",EDGE,"E25.2"),sQuery(id+"F0.wireOp",EDGE,"E25.3"),sQuery(id+"F0.wireOp",EDGE,"E25.4"),sQuery(id+"F0.wireOp",EDGE,"E25.5"),sQuery(id+"F0.wireOp",EDGE,"E25.6"),sQuery(id+"F0.wireOp",EDGE,"E25.7")])],"isStart":false});
            extrude(context, id + "F17", {"entities" : qUnion([Q0, Q1]), "endBound" : BoundingType.UP_TO_SURFACE, "endBoundEntityFace" : qUnion([Q2]), "depth" : 25 * mm});
        }
    });
